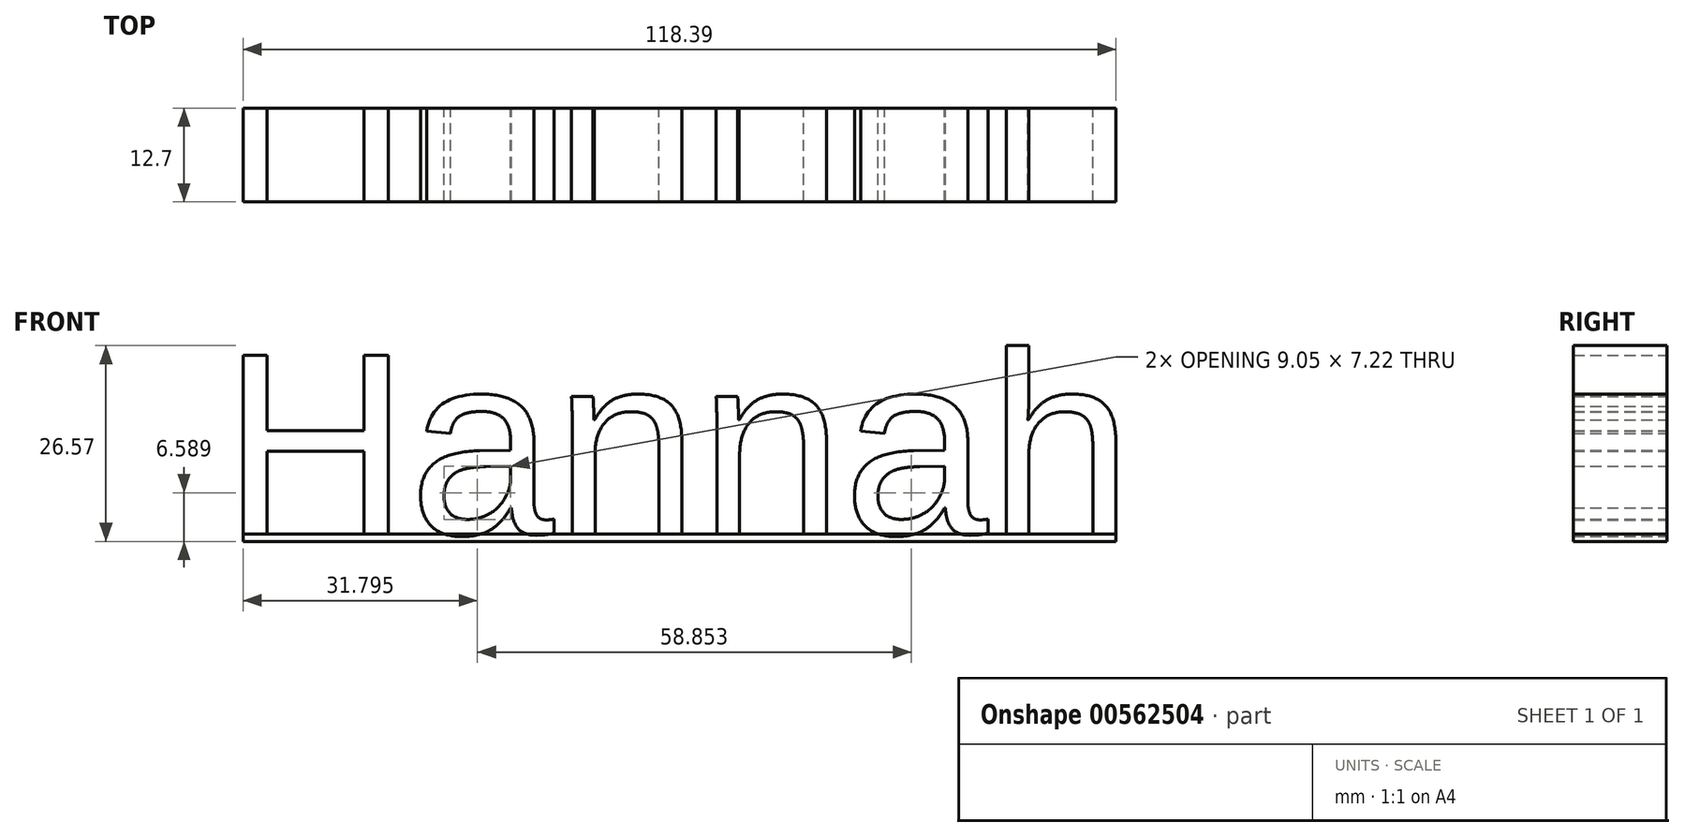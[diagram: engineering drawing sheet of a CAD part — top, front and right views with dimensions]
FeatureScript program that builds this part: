
annotation { "Feature Type Name" : "Feature", "Feature Type Description" : "" }
export const myFeature = defineFeature(function(context is Context, id is Id, definition is map)
    precondition{}
    {
        {
            var Q0;
            Q0=qCreatedBy(makeId("Front.planeOp"),FACE);
            var sketch = newSketch(context, id + "F0", { "sketchPlane" : qUnion([Q0])});
            skText(sketch, "E0", { "text": "Hannah", "fontName": "Arimo-Regular.ttf"});
            skPoint(sketch, "E1", {"position": v(0, 12.7) * mm});
            const initialGuessF0  = {"E0": [-0.06186, 0, 1, 0, 0.0254]};
            skSetInitialGuess(sketch, initialGuessF0);
            skSolve(sketch);
        }
        {
            var Q0;
            Q0=qSketchRegion(id+"F0",true);
            extrude(context, id + "F1", {"entities" : qUnion([Q0]), "endBound" : BoundingType.SYMMETRIC, "depth" : 12.7 * mm, "offsetDistance" : 25.4 * mm});
        }
        {
            var Q0;
            Q0=qCreatedBy(makeId("Top.planeOp"),FACE);
            var sketch = newSketch(context, id + "F2", { "sketchPlane" : qUnion([Q0])});
            skPoint(sketch, "E2.0", {"position": v(-58.97, 0) * mm});
            skLineSegment(sketch, "E3.0", {"start": v(-58.97, -6.35) * mm, "end": v(-58.97, 6.35) * mm});
            skLineSegment(sketch, "E4.0", {"start": v(59.42, -6.35) * mm, "end": v(59.42, 6.35) * mm});
            skLineSegment(sketch, "E5", {"start": v(-58.97, -6.35) * mm, "end": v(59.42, -6.35) * mm});
            skLineSegment(sketch, "E6", {"start": v(59.42, 6.35) * mm, "end": v(-58.97, 6.35) * mm});
            skSolve(sketch);
        }
        {
            var Q0;
            Q0=makeQuery(id+"F2.imprint","IMPRINT",FACE,{"disambiguationData":[TD([[makeQuery(id+"F2.imprint","IMPRINT",EDGE,{"derivedFrom":sQuery(id+"F2.wireOp",EDGE,"E3.0")}),-1.0]])]});
            extrude(context, id + "F3", {"entities" : qUnion([Q0]), "oppositeDirection" : true, "depth" : 1 * mm, "offsetDistance" : 25.4 * mm});
        }
    });
